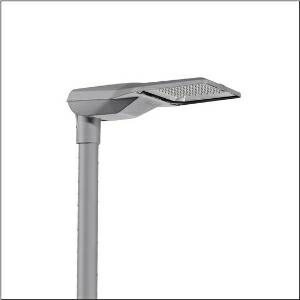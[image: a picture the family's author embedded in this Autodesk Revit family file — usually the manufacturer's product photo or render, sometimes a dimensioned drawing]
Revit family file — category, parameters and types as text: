
# Revit family: streetlight_sl_21_iq_midi___st0_8a_5xe3c21d08nb_9e73
name_source: partatom
category: Lighting Fixtures
units: mm (PartAtom-declared; Revit-internal decimal feet)

## family parameters
Cut with Voids When Loaded = No
Host = Face
Light Source = No
Part Type = Normal
Room Calculation Point = No
Round Connector Dimension = Use Diameter
Shared = No

## types (1)
- --- (1 x LED, 19210 lm, 155.5 W, 2200K)
    Apparent Load = 155 VA
    CIE Flux Codes = 41 75 97 100 100
    Color Rendering = 70
    Color Temperature = 2200K
    Default Elevation = 1800 mm
    Description = Streetlight SL 21 iQ midi, mast luminaire, primary light control with lens, of PMMA, primary optical cover: cover, of toughened safety glass, transparent, light distribution: ST0.8a, light emission: direct distribution, primary light characteristic: asymmetric, installation type: post-top, side-entry, LED, High Power LED, rated luminous flux: 19.210lm, luminous efficacy: 124lm/W, light colour: 722, colour temperature: 2200K, control gear: iQ-Comfort, control: Auto-Match, Temp-Guard, Lumen-Switch, Night-Set, Smart-Wire, Light-Fading, Desk-Remote (wireless, voltage-free reading and setting of iQ features in the workshop via application-optimized NFC function/RFID function), optimised constant luminous flux control (CLO 2.0), pre-setting: linear dimming characteristic, mains connection: 230..240V, AC, 50/60Hz, start of lifetime: 156W, end of service life: 162W, reduction: 69W, luminaire housing, of diecast aluminium, powder-coated, Siteco® metallic grey (DB 702S), corrosivity category C5 mid according to DIN EN ISO 12944, please order mast flange separately, inclination adjustable: 0°, 5°, 10°, 15°, sealing non-destructively replaceable, multi-level sealing system, length: 644mm, width: 335mm, height: 110mm, mast flange for spigot size: 42mm (side-entry): 5XC10008XM4, 60/48mm (side-entry/post-top): 5XC10108XM2, 76/60mm (side-entry/post-top): 5XC10108XM1, mounting height: 4..8m, protection rating (complete): IP66, insulation class (complete): insulation class II (safety insulation), certification: CE, ENEC, ENEC+, VDE, impact resistance: IK10, permissible operating ambient temperature for outdoor applications: -40..+50°C, standard-compliant lighting for roads and squares, packaging unit: 1 piece

Light Distribution: ST0.8a
    Height = 111 mm
    Lamp = 1 x LED
    Lamp Light Flux = 19210 lm
    Lamp Power = 155.5 W
    Lamp count = 1
    Length = 644 mm
    Luminous efficacy = 124 lm/W
    Manufacturer = Siteco
    ModVariant = No
    Model = 5XE3C21D08NB
    Number of Poles = 1
    OnlyDefault = Yes
    Power Factor = 1
    Product Name = Streetlight SL 21 iQ midi | ST0.8a
    Product group = mast luminaire | pylon top
    ProductGroupID = 6100
    Protection Class = Protection class II
    Protection Degree = IP 66
    RLX_Detail_Level = 1
    RLX_Emergency_Light_Flux = 0 lm
    RLX_Emergency_Type = 0
    RLX_Emergency_Type_DB = No
    RlxData = <blob elided: 27217 chars, md5=fb52bb1e>
    Socket = socket
    Standby Power = 0 W
    System Light Flux = 19210 lm
    System Power = 155 W
    Type Comments = factory setting: luminous flux: 100 % | dim-lin: 254 | 823 mA
    Type Image = l_1004298.jpg
    URL = http://relux.com
    VarID = @adj_169076
    Voltage = 0 V
    Weight = 0.00 kg
    Width = 336 mm

## geometry (parser evidence)
native form markers: Blend x4, Sweep x12
no freeform markers — native parametric forms only
